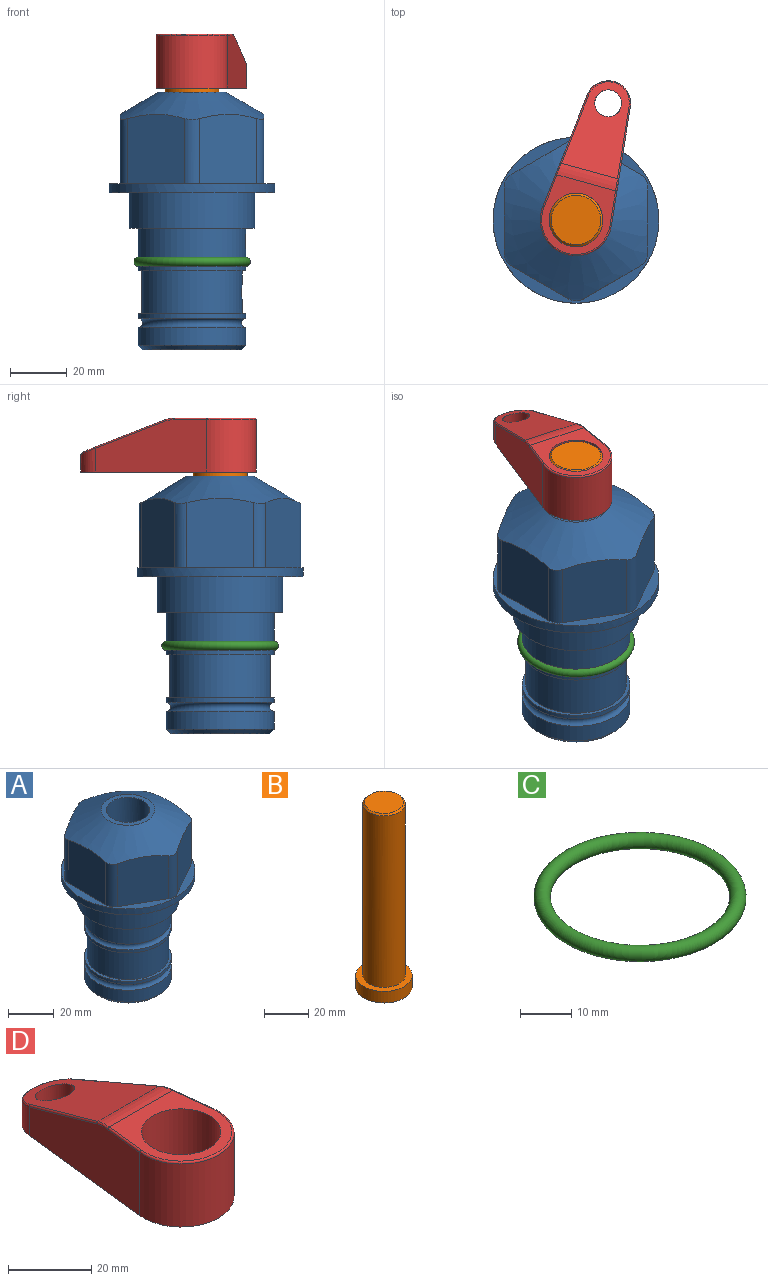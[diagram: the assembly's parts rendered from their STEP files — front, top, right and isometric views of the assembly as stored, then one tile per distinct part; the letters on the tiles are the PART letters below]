
ASSEMBLY  parts=4 mates=2
PART A: 36 faces, bbox 58.7x58.7x91.2 mm
  f0: cylinder r=17.78mm len=35.56mm, axis (0,0,1), area 1670.8mm2, adj f23,f24,f31
  f1: cylinder r=19.05mm len=38.1mm, axis (0,0,1), area 1191.9mm2, adj f26,f27,f30
  f2: plane 58.66x58.66mm, normal (0,0,-1), area 1150.6mm2, adj f3,f28
  f3: cylinder r=29.33mm len=58.66mm, axis (0,0,-1), area 585.1mm2, adj f2,f4
  f4: plane 58.66x58.66mm, normal (0,0,1), area 475.9mm2, adj f3,f5,f6,f7,f8,f9,f10,f11
  f5: plane 24.5x20.32mm, normal (0.5,-0.87,0), area 562.8mm2, adj f4,f15,f16,f17
  f6: plane 24.5x20.32mm, normal (-0.5,-0.87,0), area 562.8mm2, adj f4,f14,f15,f17
  f7: plane 24.5x23.48mm, normal (-1,0,0), area 562.8mm2, adj f4,f13,f14,f17
  f8: plane 24.5x20.32mm, normal (-0.5,0.87,0), area 562.8mm2, adj f4,f12,f13,f17
  f9: plane 24.5x20.32mm, normal (0.5,0.87,0), area 562.8mm2, adj f4,f11,f12,f17
  f10: plane 24.5x23.48mm, normal (1,0,0), area 562.8mm2, adj f4,f11,f16,f17
  f11: cylinder r=5.08mm len=23.01mm, axis (0,0,-1), area 121.2mm2, adj f4,f9,f10,f17
  f12: cylinder r=5.08mm len=23.01mm, axis (0,0,-1), area 121.2mm2, adj f4,f8,f9,f17
  f13: cylinder r=5.08mm len=23.01mm, axis (0,0,-1), area 121.2mm2, adj f4,f7,f8,f17
  f14: cylinder r=5.08mm len=23.01mm, axis (0,0,-1), area 121.2mm2, adj f4,f6,f7,f17
  f15: cylinder r=5.08mm len=23.01mm, axis (0,0,-1), area 121.2mm2, adj f4,f5,f6,f17
  f16: cylinder r=5.08mm len=23.01mm, axis (0,0,-1), area 121.2mm2, adj f4,f5,f10,f17
  f17: cone r=11.73mm half-angle=60deg, axis (0,0,-1), area 2071.8mm2, adj f5,f6,f7,f8,f9,f10,f11,f12
  f18: plane 23.46x23.46mm, normal (0,0,1), area 147.4mm2, adj f17,f35
  f19: plane 34.93x34.93mm, normal (0,0,-1), area 958mm2, adj f29
  f20: cylinder r=19.05mm len=38.1mm, axis (0,0,1), area 760.1mm2, adj f21,f29
  f21: torus R=19.05mm, axis (0,0,1), area 565.3mm2, adj f20,f22
  f22: cylinder r=19.05mm len=38.1mm, axis (0,0,1), area 190mm2, adj f21,f23
  f23: plane 38.1x38.1mm, normal (0,0,1), area 146.9mm2, adj f0,f22
  f24: plane 38.1x38.1mm, normal (0,0,-1), area 146.9mm2, adj f0,f25
  f25: cylinder r=19.05mm len=38.1mm, axis (0,0,1), area 190mm2, adj f24,f26
  f26: torus R=19.05mm, axis (0,0,1), area 565.3mm2, adj f1,f25
  f27: plane 44.45x44.45mm, normal (0,0,-1), area 411.7mm2, adj f1,f28
  f28: cylinder r=22.23mm len=44.45mm, axis (0,0,1), area 1773.5mm2, adj f2,f27
  f29: cone r=19.05mm half-angle=45deg, axis (0,0,1), area 257.5mm2, adj f19,f20
  f30: cylinder r=3.17mm len=6.75mm, axis (-1,0,0), area 128mm2, adj f1,f33
  f31: cylinder r=3.17mm len=6.35mm, axis (-1,0,0), area 102.5mm2, adj f0,f33
  f32: plane 25.4x25.4mm, normal (0,0,1), area 506.7mm2, adj f33
  f33: cylinder r=12.7mm len=66.42mm, axis (0,0,-1), area 5236.2mm2, adj f30,f31,f32,f34
  f34: cone r=9.53mm half-angle=30deg, axis (0,0,-1), area 443.4mm2, adj f33,f35
  f35: cylinder r=9.53mm len=19.05mm, axis (0,0,-1), area 849mm2, adj f18,f34
PART B: 6 faces, bbox 25.4x25.4x101.6 mm
  f0: plane 17.46x17.46mm, normal (0,0,1), area 239.5mm2, adj f5
  f1: plane 25.4x25.4mm, normal (0,0,-1), area 506.7mm2, adj f2
  f2: cylinder r=12.7mm len=25.4mm, axis (0,0,1), area 506.7mm2, adj f1,f3
  f3: plane 25.4x25.4mm, normal (0,0,1), area 221.7mm2, adj f2,f4
  f4: cylinder r=9.53mm len=94.46mm, axis (0,0,1), area 5653mm2, adj f3,f5
  f5: cone r=8.73mm half-angle=45deg, axis (0,0,-1), area 64.4mm2, adj f0,f4
PART C: 1 faces, bbox 44.7x44.7x3.2 mm
  f0: torus R=19.05mm, axis (0,0,1), area 1193.9mm2
PART D: 44 faces, bbox 27.5x64.5x19.1 mm
  f0: plane 2.3x0.95mm, normal (0,0,-1), area 1mm2, adj f25,f30,f34
  f1: plane 63.5x25.4mm, normal (0,0,-1), area 561.7mm2, adj f2,f3,f4,f5,f6,f7,f19,f20
  f2: cylinder r=12.7mm len=25.4mm, axis (0,0,-1), area 792.2mm2, adj f1,f3,f5,f13
  f3: plane 42.33x18.54mm, normal (0.99,0.11,0), area 647mm2, adj f1,f2,f4,f11,f12,f14
  f4: cylinder r=7.94mm len=15.78mm, axis (0,0,-1), area 158.6mm2, adj f1,f3,f5,f16
  f5: plane 42.33x18.54mm, normal (-0.99,0.11,0), area 647mm2, adj f1,f2,f4,f15,f17,f18
  f6: cylinder r=9.53mm len=19.05mm, axis (0,0,-1), area 1140.1mm2, adj f1,f8
  f7: cylinder r=4.76mm len=10.98mm, axis (0,0,-1), area 276.1mm2, adj f1,f9
  f8: plane 25.83x24.38mm, normal (0,0,1), area 262.2mm2, adj f6,f10,f11,f13,f15
  f9: plane 32.49x20.55mm, normal (0,0.34,0.94), area 489.9mm2, adj f7,f10,f14,f16,f18
  f10: cylinder r=12.7mm len=21.49mm, axis (-1,0,0), area 93.2mm2, adj f8,f9,f12,f17
  f11: cylinder r=0.51mm len=12.34mm, axis (0.11,-0.99,0), area 9.9mm2, adj f3,f8,f12,f13
  f12: bspline ~7.62x1.64mm, area 3.5mm2, adj f3,f10,f11,f14
  f13: torus R=12.19mm, axis (0,0,1), area 33.6mm2, adj f2,f8,f11,f15
  f14: cylinder r=0.51mm len=26.01mm, axis (0.1,-0.93,0.34), area 21.6mm2, adj f3,f9,f12,f16
  f15: cylinder r=0.51mm len=12.34mm, axis (0.11,0.99,0), area 9.9mm2, adj f5,f8,f13,f17
  f16: bspline ~15.78x7.05mm, area 15.7mm2, adj f4,f9,f14,f18
  f17: bspline ~7.62x1.64mm, area 3.5mm2, adj f5,f10,f15,f18
  f18: cylinder r=0.51mm len=26.01mm, axis (0.1,0.93,-0.34), area 21.6mm2, adj f5,f9,f16,f17
  f19: plane 21.6x14.29mm, normal (-0.99,-0.11,0), area 242.6mm2, adj f1,f26,f28,f34,f36,f38
  f20: plane 21.6x14.29mm, normal (0.99,-0.11,0), area 242.6mm2, adj f1,f27,f29,f37,f39,f41
  f21: cylinder r=12.7mm len=14.29mm, axis (0,0,-1), area 173.2mm2, adj f1,f26,f27,f30,f31,f33
  f22: cylinder r=7.94mm len=7.63mm, axis (0,0,-1), area 53.8mm2, adj f1,f28,f29,f42
  f23: plane 2.3x0.95mm, normal (0,0,-1), area 1mm2, adj f25,f33,f37
  f24: plane 17.94x12.32mm, normal (0,-0.34,-0.94), area 191.2mm2, adj f25,f38,f41,f42
  f25: cylinder r=9.53mm len=12.93mm, axis (-1,0,0), area 37.5mm2, adj f0,f23,f24,f31,f36,f39
  f26: cylinder r=1.59mm len=14.29mm, axis (0,0,-1), area 49mm2, adj f1,f19,f21,f32
  f27: cylinder r=1.59mm len=14.29mm, axis (0,0,-1), area 49mm2, adj f1,f20,f21,f35
  f28: cylinder r=1.59mm len=7.28mm, axis (0,0,-1), area 22.1mm2, adj f1,f19,f22,f40
  f29: cylinder r=1.59mm len=7.28mm, axis (0,0,-1), area 22.1mm2, adj f1,f20,f22,f43
  f30: torus R=14.29mm, axis (0,0,1), area 5.8mm2, adj f0,f21,f31,f32
  f31: bspline ~11.06x2.73mm, area 20.8mm2, adj f21,f25,f30,f33
  f32: sphere r=1.59mm, area 5.4mm2, adj f26,f30,f34
  f33: torus R=14.29mm, axis (0,0,1), area 5.8mm2, adj f21,f23,f31,f35
  f34: cylinder r=1.59mm len=1.68mm, axis (-0.11,0.99,0), area 2.4mm2, adj f0,f19,f32,f36
  f35: sphere r=1.59mm, area 5.4mm2, adj f27,f33,f37
  f36: bspline ~5.82x2.33mm, area 7.7mm2, adj f19,f25,f34,f38
  f37: cylinder r=1.59mm len=1.68mm, axis (0.11,0.99,0), area 2.4mm2, adj f20,f23,f35,f39
  f38: cylinder r=1.59mm len=18.33mm, axis (0.1,-0.93,0.34), area 46.7mm2, adj f19,f24,f36,f40
  f39: bspline ~5.82x2.33mm, area 7.7mm2, adj f20,f25,f37,f41
  f40: sphere r=1.59mm, area 3.6mm2, adj f28,f38,f42
  f41: cylinder r=1.59mm len=18.33mm, axis (0.1,0.93,-0.34), area 46.7mm2, adj f20,f24,f39,f43
  f42: bspline ~8.31x1.84mm, area 15.3mm2, adj f22,f24,f40,f43
  f43: sphere r=1.59mm, area 3.6mm2, adj f29,f41,f42
PLACE A at identity fixed
PLACE B rot(axis=(0,0,-1),15.4deg) t=(0,0,-17.64)mm
PLACE C at identity
PLACE D rot(axis=(0,0,-1),15.4deg) t=(0,0,36.97)mm
MATE cylindrical B.f2 <-> A.f0  axis (0,0,1) through (0,0,8)mm
MATE fastened D.f2 <-> B.f2  axis (0,0,-1) through (0,0,56.02)mm
